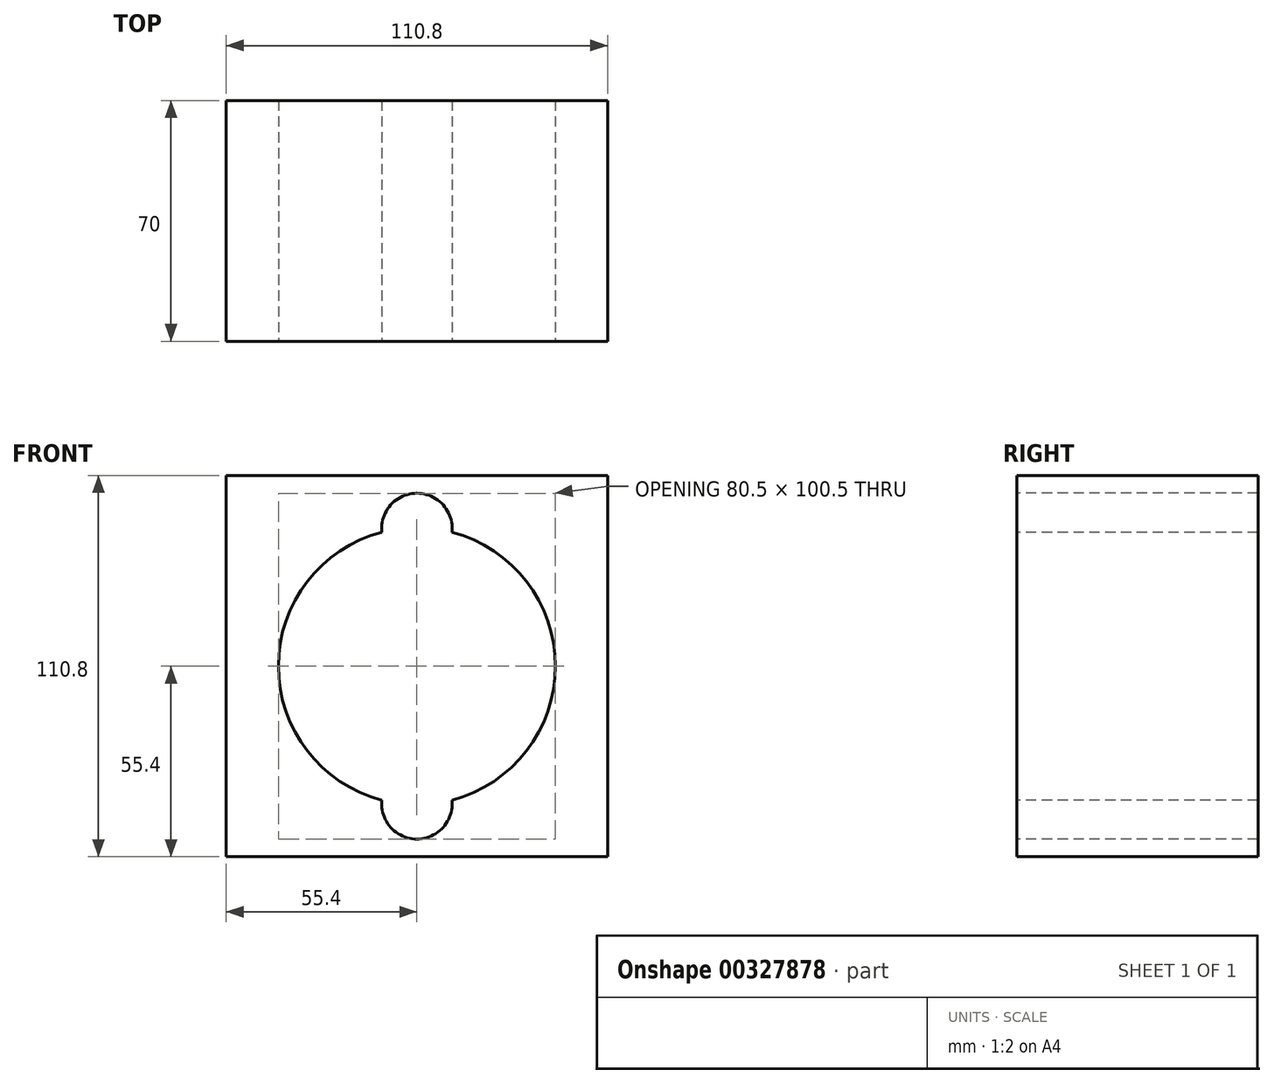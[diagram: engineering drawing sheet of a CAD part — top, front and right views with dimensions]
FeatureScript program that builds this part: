
annotation { "Feature Type Name" : "Feature", "Feature Type Description" : "" }
export const myFeature = defineFeature(function(context is Context, id is Id, definition is map)
    precondition{}
    {
        {
            var Q0;
            Q0=qCreatedBy(makeId("Front.planeOp"),FACE);
            var sketch = newSketch(context, id + "F0", { "sketchPlane" : qUnion([Q0])});
            skCircle(sketch, "E0", {"center": v(0, 0) * mm, "radius": 40.25 * mm});
            skLineSegment(sketch, "E1", {"start": v(0, 0) * mm, "end": v(0, -40.25) * mm, "construction": true});
            skLineSegment(sketch, "E2", {"start": v(0, 0) * mm, "end": v(40.25, 0) * mm, "construction": true});
            skLineSegment(sketch, "E3.bottom", {"start": v(-55.4, 55.4) * mm, "end": v(55.4, 55.4) * mm});
            skLineSegment(sketch, "E3.top", {"start": v(-55.4, -55.4) * mm, "end": v(55.4, -55.4) * mm});
            skLineSegment(sketch, "E3.left", {"start": v(-55.4, 55.4) * mm, "end": v(-55.4, -55.4) * mm});
            skLineSegment(sketch, "E3.right", {"start": v(55.4, 55.4) * mm, "end": v(55.4, -55.4) * mm});
            skCircle(sketch, "E4", {"center": v(0, 0) * mm, "radius": 40 * mm, "construction": true});
            skCircle(sketch, "E5", {"center": v(0, 40) * mm, "radius": 10.25 * mm});
            skCircle(sketch, "E6", {"center": v(0, -40) * mm, "radius": 10.25 * mm});
            skLineSegment(sketch, "E7", {"start": v(0, 50.25) * mm, "end": v(0, -50.25) * mm, "construction": true});
            skSolve(sketch);
        }
        {
            var Q0;
            Q0=makeQuery(id+"F0.imprint","IMPRINT",FACE,{"disambiguationData":[TD([[makeQuery(id+"F0.imprint","IMPRINT",EDGE,{"derivedFrom":sQuery(id+"F0.wireOp",EDGE,"E3.bottom")}),-1.0]])]});
            extrude(context, id + "F1", {"entities" : qUnion([Q0]), "oppositeDirection" : true, "depth" : 70 * mm});
        }
    });
